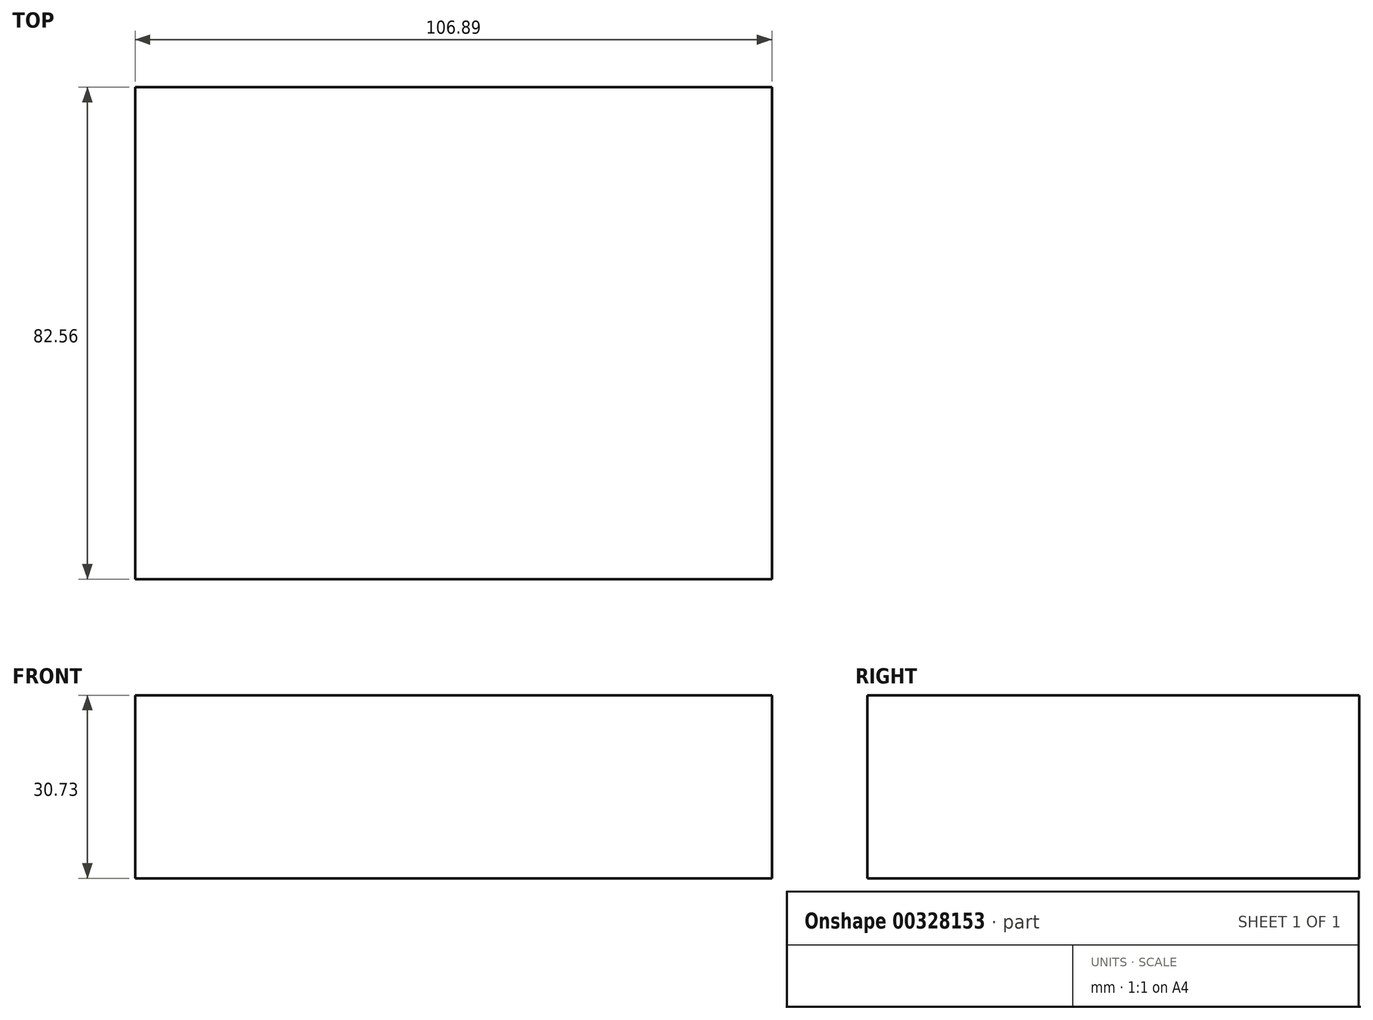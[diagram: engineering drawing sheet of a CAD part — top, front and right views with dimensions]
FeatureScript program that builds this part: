
annotation { "Feature Type Name" : "Feature", "Feature Type Description" : "" }
export const myFeature = defineFeature(function(context is Context, id is Id, definition is map)
    precondition{}
    {
        {
            var Q0;
            Q0=qCreatedBy(makeId("Top.planeOp"),FACE);
            var sketch = newSketch(context, id + "F0", { "sketchPlane" : qUnion([Q0])});
            skLineSegment(sketch, "E0.bottom", {"start": v(-57.34, 42) * mm, "end": v(49.55, 42) * mm});
            skLineSegment(sketch, "E0.top", {"start": v(-57.34, -40.55) * mm, "end": v(49.55, -40.55) * mm});
            skLineSegment(sketch, "E0.left", {"start": v(-57.34, 42) * mm, "end": v(-57.34, -40.55) * mm});
            skLineSegment(sketch, "E0.right", {"start": v(49.55, 42) * mm, "end": v(49.55, -40.55) * mm});
            skSolve(sketch);
        }
        {
            var Q0;
            Q0 = qSketchRegion(id + "F0", true);
            extrude(context, id + "F1", {"entities" : qUnion([Q0]), "depth" : 30.73 * mm});
        }
    });
